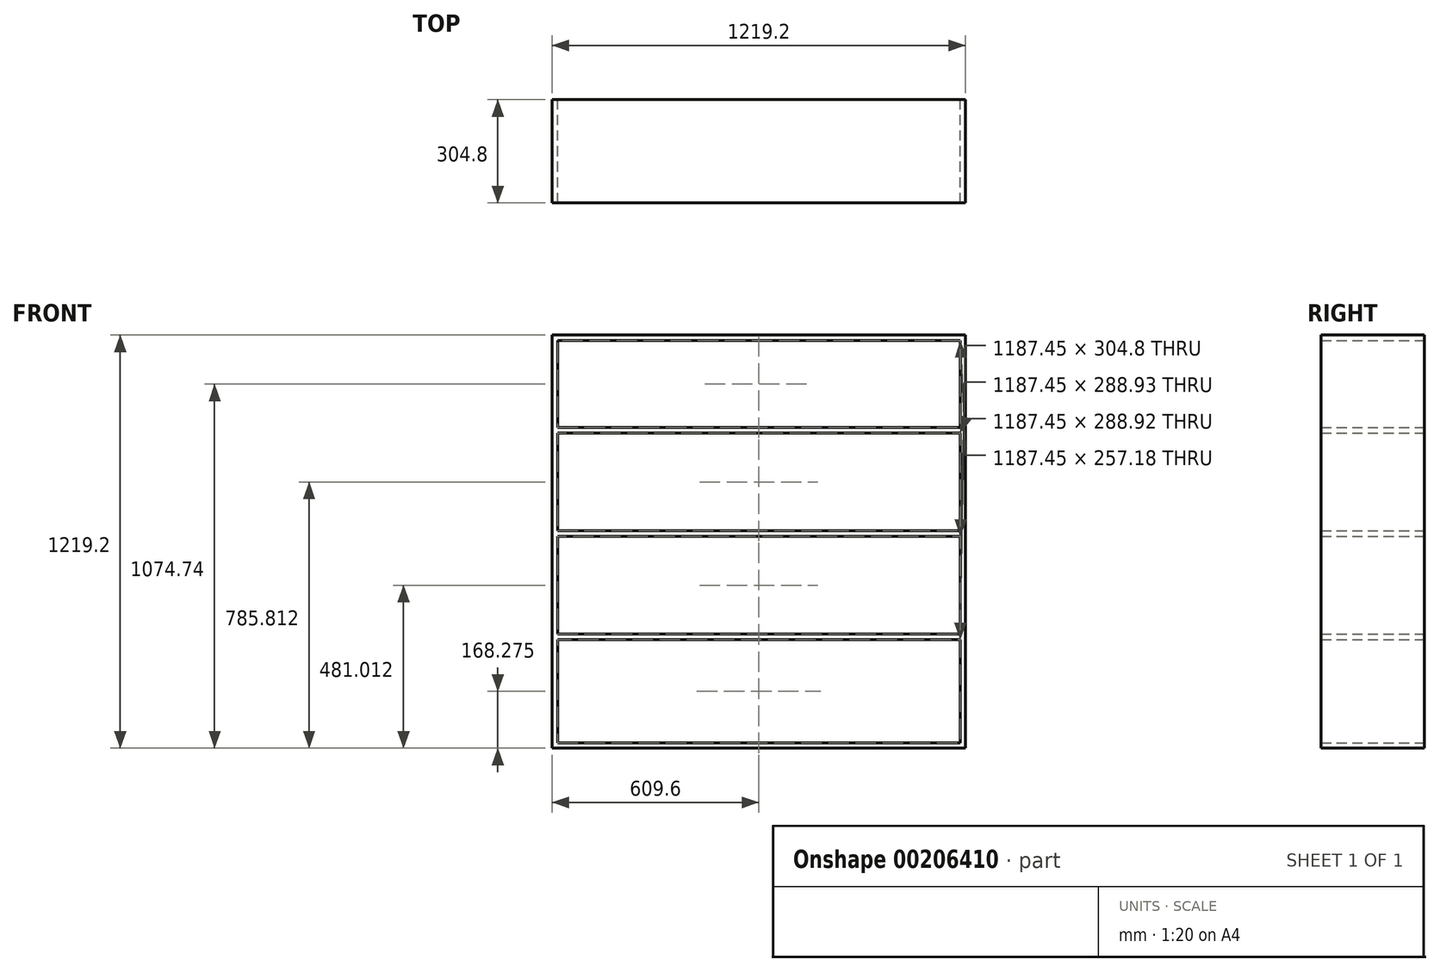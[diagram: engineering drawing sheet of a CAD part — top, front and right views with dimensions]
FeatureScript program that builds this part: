
annotation { "Feature Type Name" : "Feature", "Feature Type Description" : "" }
export const myFeature = defineFeature(function(context is Context, id is Id, definition is map)
    precondition{}
    {
        {
            var Q0;
            Q0=qCreatedBy(makeId("Front.planeOp"),FACE);
            var sketch = newSketch(context, id + "F0", { "sketchPlane" : qUnion([Q0])});
            skLineSegment(sketch, "E0.bottom", {"start": v(-1219.2, 1219.2) * mm, "end": v(0, 1219.2) * mm});
            skLineSegment(sketch, "E0.top", {"start": v(-1219.2, 0) * mm, "end": v(0, 0) * mm});
            skLineSegment(sketch, "E0.left", {"start": v(-1219.2, 1219.2) * mm, "end": v(-1219.2, 0) * mm});
            skLineSegment(sketch, "E0.right", {"start": v(0, 1219.2) * mm, "end": v(0, 0) * mm});
            skLineSegment(sketch, "E1.bottom", {"start": v(-1203.33, 1203.33) * mm, "end": v(-15.88, 1203.33) * mm});
            skLineSegment(sketch, "E1.top", {"start": v(-1203.33, 15.88) * mm, "end": v(-15.88, 15.88) * mm});
            skLineSegment(sketch, "E1.left", {"start": v(-1203.33, 1203.33) * mm, "end": v(-1203.33, 15.88) * mm});
            skLineSegment(sketch, "E1.right", {"start": v(-15.88, 1203.33) * mm, "end": v(-15.88, 15.88) * mm});
            skLineSegment(sketch, "E2.bottom", {"start": v(-1203.33, 336.55) * mm, "end": v(-15.87, 336.55) * mm});
            skLineSegment(sketch, "E2.top", {"start": v(-1203.33, 320.68) * mm, "end": v(-15.87, 320.68) * mm});
            skLineSegment(sketch, "E2.left", {"start": v(-1203.33, 336.55) * mm, "end": v(-1203.33, 320.68) * mm});
            skLineSegment(sketch, "E2.right", {"start": v(-15.88, 336.55) * mm, "end": v(-15.88, 320.68) * mm});
            skLineSegment(sketch, "E3.0.1.0", {"start": v(-1203.33, 625.48) * mm, "end": v(-15.87, 625.48) * mm});
            skLineSegment(sketch, "E3.0.1.1", {"start": v(-1203.33, 641.35) * mm, "end": v(-15.87, 641.35) * mm});
            skLineSegment(sketch, "E3.0.2.0", {"start": v(-1203.33, 930.27) * mm, "end": v(-15.87, 930.27) * mm});
            skLineSegment(sketch, "E3.0.2.1", {"start": v(-1203.33, 946.15) * mm, "end": v(-15.87, 946.15) * mm});
            skLineSegment(sketch, "E3.direction1", {"start": v(-1203.33, 320.68) * mm, "end": v(-1178.33, 320.68) * mm, "construction": true});
            skLineSegment(sketch, "E3.direction2", {"start": v(-1203.33, 320.68) * mm, "end": v(-1203.33, 625.48) * mm, "construction": true});
            skSolve(sketch);
        }
        {
            var Q0;
            Q0 = qSketchRegion(id + "F0", true);
            var Q1;
            {var subQ0=sQuery(id+"F0.wireOp",EDGE,"E3.0.2.0");Q1=makeQuery(id+"F0.imprint","IMPRINT",FACE,{"disambiguationData":[TD([[makeQuery(id+"F0.imprint","IMPRINT",EDGE,{"derivedFrom":subQ0}),1.0]])]});}
            var Q2;
            {var subQ0=sQuery(id+"F0.wireOp",EDGE,"E3.0.1.0");Q2=makeQuery(id+"F0.imprint","IMPRINT",FACE,{"disambiguationData":[TD([[makeQuery(id+"F0.imprint","IMPRINT",EDGE,{"derivedFrom":subQ0}),1.0]])]});}
            var Q3;
            Q3=makeQuery(id+"F0.imprint","IMPRINT",FACE,{"disambiguationData":[TD([[makeQuery(id+"F0.imprint","IMPRINT",EDGE,{"derivedFrom":sQuery(id+"F0.wireOp",EDGE,"E2.bottom")}),-1.0]])]});
            extrude(context, id + "F1", {"entities" : qUnion([Q0, Q1, Q2, Q3]), "depth" : 304.8 * mm});
        }
    });
